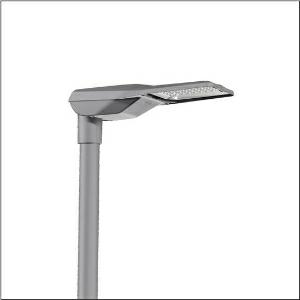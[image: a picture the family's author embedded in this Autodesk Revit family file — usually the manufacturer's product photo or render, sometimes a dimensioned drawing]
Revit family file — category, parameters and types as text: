
# Revit family: streetlight_sl_21_iq_mini___pl52_5xe2h41d08hb_c209
name_source: partatom
category: Lighting Fixtures
units: mm (PartAtom-declared; Revit-internal decimal feet)

## family parameters
Cut with Voids When Loaded = No
Host = Face
Light Source = No
Part Type = Normal
Room Calculation Point = No
Round Connector Dimension = Use Diameter
Shared = No

## types (1)
- --- (1 x LED, 9690 lm, 70.9 W, 4000K)
    Apparent Load = 71 VA
    CIE Flux Codes = 27 59 98 100 100
    Color Rendering = 70
    Color Temperature = 4000K
    Default Elevation = 1800 mm
    Description = Streetlight SL 21 iQ mini, mast luminaire, primary light control with lens, of PMMA, primary optical cover: cover, of toughened safety glass, transparent, light distribution: PL52, light emission: direct distribution, primary light characteristic: asymmetric, installation type: post-top, side-entry, LED, High Power LED, rated luminous flux: 9.690lm, luminous efficacy: 137lm/W, light colour: 740, colour temperature: 4000K, control gear: iQ-Comfort, control: Auto-Match, Temp-Guard, Lumen-Switch, Night-Set, Smart-Wire, Light-Fading, Desk-Remote (wireless, voltage-free reading and setting of iQ features in the workshop via application-optimized NFC function/RFID function), optimised constant luminous flux control (CLO 2.0), pre-setting: linear dimming characteristic, mains connection: 220..240V, AC, 50/60Hz, start of lifetime: 71W, end of service life: 75W, reduction: 31W, luminaire housing, of diecast aluminium, powder-coated, SITECO metallic grey (DB 702S), corrosivity category C5 high according to DIN EN ISO 12944, please order mast flange separately, inclination adjustable: 0°, 5°, 10°, 15°, sealing non-destructively replaceable, multi-level sealing system, length: 628mm, width: 235mm, height: 110mm, mast flange for spigot size: 42mm (side-entry): 5XC10008XM4, 60/48mm (side-entry/post-top): 5XC10108XM2, 76/60mm (side-entry/post-top): 5XC10108XM1, mounting height: 4..8m, protection rating (complete): IP66, insulation class (complete): insulation class II (safety insulation), certification: CE, ENEC, ENEC+, VDE, impact resistance: IK10, permissible operating ambient temperature for outdoor applications: -40..+50°C, standard-compliant lighting for roads and squares, packaging unit: 1 piece

Light Distribution: PL52
    Height = 110 mm
    Lamp = 1 x LED
    Lamp Light Flux = 9690 lm
    Lamp Power = 70.9 W
    Lamp count = 1
    Length = 625 mm
    Luminous efficacy = 137 lm/W
    Manufacturer = Siteco
    ModVariant = No
    Model = 5XE2H41D08HB
    Number of Poles = 1
    OnlyDefault = Yes
    Power Factor = 1
    Product Name = Streetlight SL 21 iQ mini | PL52
    Product group = mast luminaire | pylon top
    ProductGroupID = 6100
    Protection Class = Protection class II
    Protection Degree = IP 66
    RLX_Detail_Level = 1
    RLX_Emergency_Light_Flux = 0 lm
    RLX_Emergency_Type = 0
    RLX_Emergency_Type_DB = No
    RlxData = <blob elided: 35929 chars, md5=a653811e>
    Socket = socket
    Standby Power = 0 W
    System Light Flux = 9690 lm
    System Power = 71 W
    Type Comments = factory setting: luminous flux: 100 % | dim-lin: 254 | 711 mA
    Type Image = l_1003519.jpg
    URL = http://relux.com
    VarID = @adj_157869
    Voltage = 0 V
    Weight = 0.00 kg
    Width = 234 mm

## geometry (parser evidence)
native form markers: Blend x4, Sweep x9
no freeform markers — native parametric forms only
